# Revit family: C_WTS2-275_2DO_CAD_MULT_Prod
name_source: partatom
category: Detail Items
revit_build: Autodesk Revit 2015 (Build: 20140606_1530(x64)
units: mm (PartAtom-declared; Revit-internal decimal feet)

## types (3) — shared parameters
Density = 0.03 kg
Description = Connector Other
EPD = https://www.strongtie.eu
ETA / DoP = https://www.strongtie.eu
Manufacturer = Simpson Strong-Tie
Model = WTS2-275
Model Disclaimer = Contact Simpson Strong-Tie Company  for more information
Model ID = 0141612898263614564840517991598580651282
Name = WTS2-275
ObjectType = WTS2-275
Product Material = Stainless steel A2
Product Type = Connector Other
Reference = WTS2-275
Technical datasheet = https://www.strongtie.eu
URL = www.strongtie.eu
UniClass Number = Pr_20_29_31_44
UniClass Title = Joist hangers
_visibleright = No

## per-type parameters (varying)
| type | _visiblefront | _visibleleft | _visibletop |
| SST_WTS2-275_Front | Yes | No | No |
| SST_WTS2-275_Top | No | No | Yes |
| SST_WTS2-275_Left | No | Yes | No |

## geometry (parser evidence)
native form markers: Sweep x2
no freeform markers — native parametric forms only
